# Revit family: IS_Connect_B0687_BIM_DE
name_source: partatom
category: Plumbing Fixtures
revit_build: Autodesk Revit MEP 2016 (Build: 20161004_0715(x64)
units: mm (PartAtom-declared; Revit-internal decimal feet)

## family parameters
Always vertical = No
Cut with Voids When Loaded = Yes
OmniClass Number = 23.45.55.17
OmniClass Title = Mixing Faucets
Part Type = Normal
Room Calculation Point = No
Round Connector Dimension = Use Diameter
Shared = No
Work Plane-Based = No

## types (2) — shared parameters
Accessories = www.idealstandard.de\ersatzteile
AssetType = Fixed
BIMobject category = Taps & Mixers
BOSUseNativeGeometries = 1
Brand = Ideal Standard
Brand url = http://www.idealstandard.de
CodePerformance = 0
ConnectionType = Plumbing
CurrencyUnit = €
CurrentRevision = 1
DurationUnit = Jaar
Edition number = 1
ExpectedLife = 25
FaucetFunction = mixed
FaucetOperation = leverhandle
FaucetType = pillar
Features = CONNECT kitchen mixer one hole single lever hand
IFC Classification = Sanitary Terminal
IfcExportAs = Sanitary terminal type
IfcExportType = KITCHEN TAP
Installation instructions = http://www.idealstandard.de
InstallationInstructions = www.idealstandard.de\produkte
LinearUnits = millimetres
MaintenanceInformation = www.idealstandard.de
Manufacturer = http://www.idealstandard.de
Manufacturer name = Ideal Standard
ManufacturerURL = http://www.idealstandard.de
Material = Brass
Material main = Brass
NBS Reference Code = 35-79-79
NBS Reference Description = Sink Water Supply Fittings
NettWeight = 2,461 kg
NominalHeight = 296 mm
NominalLength = 234 mm
NominalWidth = 111 mm
OmniClass Code = 23-31 11 00
OmniClass Description = Faucets
Product Guid = d0b05bda-d032-4f87-9392-2c9f2a3ad38c
Product SKU = B0687
Product certification = 0
Product data url = https://bimobject.com
Product family = CONNECT
Product group = Kitchen Mixer
Product name = CONNECT kitchen mixer one hole single lever hand
Product url = http://www.idealstandard.de
ProductInformation = www.idealstandard.de/produkte
QR code = http://bimobject.com
Shape = Sculptured
Size = 296 x 234 x 111mm
Space = Internal
SpareParts = www.idealstandard.de/ersatzteile
Technical description = http://www.idealstandard.de
TestPressure = 10 Bar
URL = http://www.idealstandard.de
Uniclass 1.4 Code = L8212
Uniclass 1.4 Description = Fittings
Uniclass 2.0 Code = PR-35-79-79
Uniclass 2.0 Description = Sink Water Supply Fittings
Uniclass 2015 Code = Pr_40_20_87_82
Uniclass 2015 Name = Sink manual water supply sets
Uniclass2015Code = Pr_40_20_87_84
Uniclass2015Title = Sink taps
Uniclass2015Version = Products v1.1
ValveMechanism = ceramic disc
ValveOperation = lever
VolumeUnits = Litres
Weight Net (Kg) = 2.46
WorkingPressure = 1-5 Bar
zero-valued in all types: Cost, Nominal height, Nominal width

## per-type parameters (varying)
| type | BIMObjectName | BarCode | Color | Description | EAN code | Finish | MainColor | MainMaterial | Model | ModelNumber | ModelReference | Name |
| B0687AA - CONNECT kitchen mixer one hole single lever hand | ISI_IdealStandard_SinkTaps_CONNECT_B0687AA | 3800861045533 | Chrome | B0687AA CONNECT kitchen mixer one hole single lever hand | https://3800861045533 | Chrome | Chrome | IS_RenderMaterial_ChromePolished | B0687AA | B0687AA | B0687AA CONNECT kitchen mixer one hole single lever hand | ISI_IdealStandard_SinkTaps_CONNECT_B0687AA |
| B0687GN - CONNECT kitchen mixer one hole single lever hand | ISI_IdealStandard_SinkTaps_CONNECT_B0687GN | 3800861045540 | Ultra Steel | B0687GN CONNECT kitchen mixer one hole single lever hand | https://3800861045540 | Ultra Steel | Ultra Steel | IS_RenderMateriat_UltraSteel | B0687GN | B0687GN | B0687GN CONNECT kitchen mixer one hole single lever hand | ISI_IdealStandard_SinkTaps_CONNECT_B0687GN |

## geometry (parser evidence)
native form markers: Blend x2, Sweep x2
no freeform markers — native parametric forms only
